# Revit family: VLGFS1002-xxxWS8xxBQPxxxx
name_source: partatom
category: Oprawy oświetleniowe
revit_build: Autodesk Revit 2017 (Build: 20190507_1515(x64)
units: mm (PartAtom-declared; Revit-internal decimal feet)

## family parameters
Numer OmniClass = 23.80.70.11
Obiekt nadrzędny = Powierzchnia
Punkt obliczania pomieszczeń = Nie
Tnij formami wycięć po wczytaniu = Nie
Typ części = Normalny
Tytuł OmniClass = Luminaries for Internal Lighting
Współdzielony = Nie
Wymiar okrągłego złącza = Użyj średnicy
Źródło światła = Tak

## types (8) — shared parameters
Emituj kształt widoczny w renderingu = Nie
Emituj z długości prostokąta = 94 mm  [stored 0.308399 ft]
Emituj z szerokości prostokąta = 977 mm  [stored 3.20538 ft]
Filtr koloru = 16777215
Kod zespołu = D5020200
Lampa = LED
Obciążenie pozorne = 78 VA
Odchylenie kierunku = 90.00°
Plik sieci fotometrycznej = VLGFS1502-5NDWS840BQP1500.IES
Producent = RIDI Leuchten GmbH
URL = www.ridi.de
Zmiana temperatury barwowej przyciemniania lampy = <Brak>
brand = RIDI
conformity mark = CE
electrical safety class = 1
height = 74 mm  [stored 0.242782 ft]
ingress protection (IP) code = IP54
length = 1000 mm  [stored 3.28084 ft]
nominal frequency = 50-60Hz
nominal voltage = 230
rated input power = 78
voltage type (AC, DC, UC) = AC
weight = 2.2 kg
width = 97 mm  [stored 0.318241 ft]
zero-valued in all types: Domyślna rzędna

## per-type parameters (varying)
| type | Model |
| VLGFS1002-5NDWS830BQP0950 | 1551250 |
| VLGFS1002-7DAWS830BQP0950 | 1561250 |
| VLGFS1002-5NDWS840BQP1000 | 1551247 |
| VLGFS1002-7DAWS840BQP1000 | 1561247 |
| VLGFS1002-5NDWS850BQP1000 | 1551253 |
| VLGFS1002-7DAWS850BQP1000 | 1561253 |
| VLGFS1002-5NDWS865BQP1000 | 1551256 |
| VLGFS1002-7DAWS865BQP1000 | 1561256 |

note: column(s) folded — value = type name in every type: product name

note: [stored X ft] marks values corroborated as IEEE doubles in the binary element streams (Revit-internal decimal feet)
